# Revit family: KS ALU-PU 80 -s-, DS 40, M10-M12, Ø 60,3- 88,9
name_source: partatom
category: HLS-Bauteile
revit_build: Autodesk Revit 2017 (Build: 20190507_1515(x64)
units: mm (PartAtom-declared; Revit-internal decimal feet)

## family parameters
Arbeitsebenenbasiert = Ja
Beim Laden mit Abzugskörper schneiden = Nein
Bemaßung runder Anschluss = Durchmesser verwenden
Gemeinsam genutzt = Ja
Immer vertikal = Nein
Raumberechnungspunkt = Nein
Teiletyp = Normal

## types (5) — shared parameters
A = 65 mm
Anschluss = M10/M12
BP = 14 mm  [stored 0.0459318 ft]
Baustoffklasse = B2
DS = 40 mm  [stored 0.131234 ft]
DVS = 7 mm  [stored 0.0229659 ft]
Dichte Kern = 80 kg/m³
Dichte Mantel = 2.700 kg/m³
Dicke Mantel = 0,08 mm
Dämmkörper = ALU/PU
Dämmstärke = 40 mm  [stored 0.131234 ft]
Fabrikat = MEFA
Firma = MEFA Befestigungs- und Montagesysteme GmbH
HGA = 22 mm  [stored 0.0721785 ft]
Kurztext1 = Kälteschelle RG80s ALU/PU
L Ü Bogen = 19 mm  [stored 0.062336 ft]
MD = 3 mm  [stored 0.00984252 ft]
Material = Stahl
Material Mantel = Alufolie
Mengeneinheit = St
Oberflaeche = galvanisch verzinkt
Vorgabe-Ansicht = 1219 mm
Wasserdampfdiffusionswiderstand = 18750 µ
Wärmeleitfähigkeit = 0.025 W/mK
d1 = 7 mm  [stored 0.0229659 ft]
max. Temperaturbeständigkeit = 120 °C
mittl. Nenndruckfestigkeit Kern = 0,5 N/mm²
stat. Belastung Kern = 0,1 N/mm²
vpe = 1 St

## per-type parameters (varying)
- Kälteschelle ALU-PU 80 -s-, DS 40, M10/M12, Ø 60,3: AB=2 mm  [stored 0.00656168 ft]; Anschlußhöhe=65 mm; Artikelnummer=71506042; B=186 mm; Breite=203 mm; D=60 mm; D0=140 mm; DF1=19 mm  [stored 0.062336 ft]; DF2=19 mm  [stored 0.062336 ft]; Dmax=62 mm  [stored 0.203412 ft]; Dmin=58 mm  [stored 0.190289 ft]; EAN=4250928441768; Gewicht=0.57 kg; Gewicht pro Bauteil=0.57 kg; H=168 mm; Kurztext2=60,3 mm Iso 40 x 50 mm M10/M12; L=50 mm  [stored 0.164042 ft]; MB=30 mm  [stored 0.0984252 ft]; Materialname=S235; R=70 mm  [stored 0.229659 ft]; RM=73 mm; Rohraußendurchmesser Stahl=60,3 mm; Rohrschellentyp=Maxima PSM; S=167 mm  [stored 0.5479 ft]; S1=159 mm; Schalenlänge=50 mm; max. zul. Last=0.40 kN
- Kälteschelle ALU-PU 80 -s-, DS 40, M10/M12, Ø 63,5: AB=2 mm  [stored 0.00656168 ft]; Anschlußhöhe=66 mm; Artikelnummer=71506450; B=189 mm; Breite=192 mm; D=64 mm  [stored 0.209974 ft]; D0=144 mm; DF1=20 mm  [stored 0.0656168 ft]; DF2=19 mm  [stored 0.062336 ft]; Dmax=64 mm  [stored 0.209974 ft]; Dmin=62 mm  [stored 0.203412 ft]; EAN=4250928441775; Gewicht=0.42 kg; Gewicht pro Bauteil=0.42 kg; H=172 mm; Kurztext2=63,5 mm Iso 40 x 50 mm M10/M12; L=50 mm  [stored 0.164042 ft]; MB=25 mm  [stored 0.082021 ft]; Materialname=DD11; R=72 mm  [stored 0.23622 ft]; RM=75 mm; Rohraußendurchmesser Stahl=63,5 mm; Rohrschellentyp=Omnia MB; S=169 mm; S1=163 mm; Schalenlänge=50 mm; max. zul. Last=0.50 kN
- Kälteschelle ALU-PU 80 -s-, DS 40, M10/M12, Ø 70: AB=2 mm  [stored 0.00656168 ft]; Anschlußhöhe=65 mm; Artikelnummer=71607050; B=198 mm; Breite=197 mm; D=70 mm  [stored 0.229659 ft]; D0=150 mm; DF1=20 mm  [stored 0.0656168 ft]; DF2=20 mm  [stored 0.0656168 ft]; Dmax=72 mm  [stored 0.23622 ft]; Dmin=68 mm; EAN=4250928441782; Gewicht=0.46 kg; Gewicht pro Bauteil=0.46 kg; H=178 mm; Kurztext2=70 mm Iso 40 x 66 mm M10/M12; L=66 mm  [stored 0.216535 ft]; MB=25 mm  [stored 0.082021 ft]; Materialname=DD11; R=75 mm; RM=78 mm  [stored 0.255906 ft]; Rohraußendurchmesser Stahl=70 mm; Rohrschellentyp=Omnia MB; S=178 mm; S1=169 mm; Schalenlänge=66 mm; max. zul. Last=0.50 kN
- Kälteschelle ALU-PU 80 -s-, DS 40, M10/M12, Ø 76,1: AB=1 mm  [stored 0.00328084 ft]; Anschlußhöhe=65 mm; Artikelnummer=71607642; B=206 mm; Breite=219 mm; D=76 mm; D0=156 mm; DF1=21 mm  [stored 0.0688976 ft]; DF2=21 mm  [stored 0.0688976 ft]; Dmax=78 mm  [stored 0.255906 ft]; Dmin=75 mm; EAN=4250928441805; Gewicht=0.59 kg; Gewicht pro Bauteil=0.59 kg; H=184 mm; Kurztext2=76,1 mm Iso 40 x 66 mm M10/M12; L=66 mm  [stored 0.216535 ft]; MB=30 mm  [stored 0.0984252 ft]; Materialname=S235; R=78 mm  [stored 0.255906 ft]; RM=81 mm; Rohraußendurchmesser Stahl=76,1 mm; Rohrschellentyp=Maxima PSM; S=185 mm; S1=175 mm; Schalenlänge=66 mm; max. zul. Last=0.60 kN
- Kälteschelle ALU-PU 80 -s-, DS 40, M10/M12, Ø 88,9: AB=1 mm  [stored 0.00328084 ft]; Anschlußhöhe=65 mm; Artikelnummer=75408950; B=218 mm; Breite=219 mm; D=89 mm; D0=169 mm; DF1=21 mm  [stored 0.0688976 ft]; DF2=21 mm  [stored 0.0688976 ft]; Dmax=90 mm  [stored 0.295276 ft]; Dmin=88 mm  [stored 0.288714 ft]; EAN=4250928443205; Gewicht=0.54 kg; Gewicht pro Bauteil=0.54 kg; H=197 mm; Kurztext2=88,9 mm Iso 40 x 83 mm M10/M12; L=83 mm  [stored 0.27231 ft]; MB=25 mm  [stored 0.082021 ft]; Materialname=DD11; R=84 mm; RM=87 mm; Rohraußendurchmesser Stahl=88,9 mm; Rohrschellentyp=Omnia MB; S=197 mm; S1=188 mm; Schalenlänge=83 mm; max. zul. Last=0.60 kN

note: [stored X ft] marks values corroborated as IEEE doubles in the binary element streams (Revit-internal decimal feet)

## geometry (parser evidence)
native form markers: Sweep x1
no freeform markers — native parametric forms only
